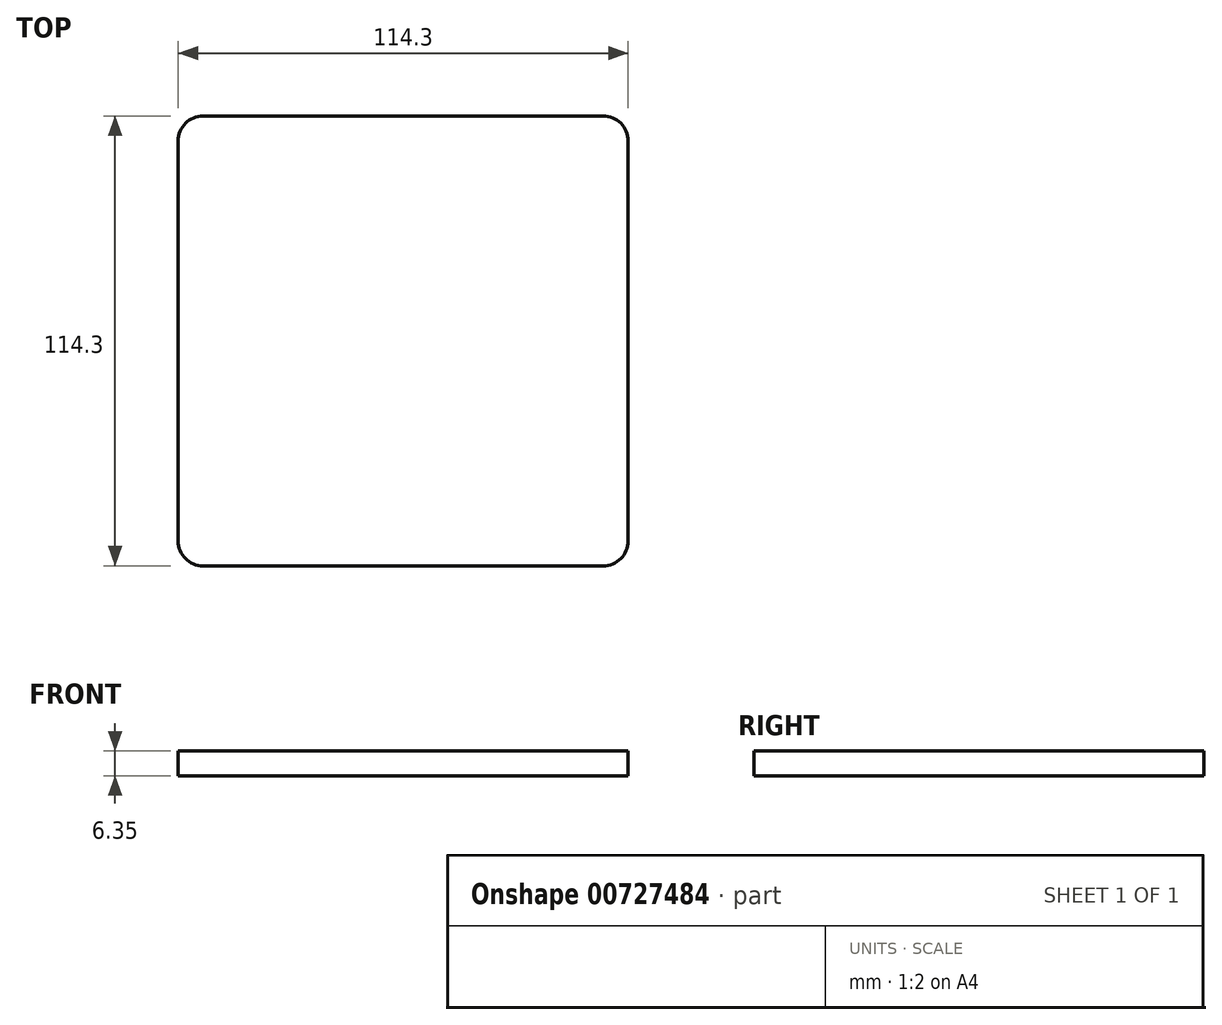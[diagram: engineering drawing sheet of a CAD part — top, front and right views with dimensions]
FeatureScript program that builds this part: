
annotation { "Feature Type Name" : "Feature", "Feature Type Description" : "" }
export const myFeature = defineFeature(function(context is Context, id is Id, definition is map)
    precondition{}
    {
        {
            var Q0;
            Q0=qCreatedBy(makeId("Top.planeOp"),FACE);
            var sketch = newSketch(context, id + "F0", { "sketchPlane" : qUnion([Q0])});
            skLineSegment(sketch, "E0.bottom", {"start": v(50.8, -57.15) * mm, "end": v(-50.8, -57.15) * mm});
            skLineSegment(sketch, "E0.top", {"start": v(50.8, 57.15) * mm, "end": v(-50.8, 57.15) * mm});
            skLineSegment(sketch, "E0.left", {"start": v(57.15, -50.8) * mm, "end": v(57.15, 50.8) * mm});
            skLineSegment(sketch, "E0.right", {"start": v(-57.15, -50.8) * mm, "end": v(-57.15, 50.8) * mm});
            skPoint(sketch, "E0.middle", {"position": v(0, 0) * mm});
            skPoint(sketch, "E1.visualSharp", {"position": v(-57.15, 57.15) * mm});
            skArc(sketch, "E1.filletArc", {"start": v(-50.8, 57.15) * mm, "mid": v(-55.3, 55.3) * mm, "end": v(-57.15, 50.8) * mm});
            skPoint(sketch, "E2.visualSharp", {"position": v(57.15, 57.15) * mm});
            skArc(sketch, "E2.filletArc", {"start": v(57.15, 50.8) * mm, "mid": v(55.3, 55.3) * mm, "end": v(50.8, 57.15) * mm});
            skPoint(sketch, "E3.visualSharp", {"position": v(57.15, -57.15) * mm});
            skArc(sketch, "E3.filletArc", {"start": v(50.8, -57.15) * mm, "mid": v(55.3, -55.3) * mm, "end": v(57.15, -50.8) * mm});
            skPoint(sketch, "E4.visualSharp", {"position": v(-57.15, -57.15) * mm});
            skArc(sketch, "E4.filletArc", {"start": v(-57.15, -50.8) * mm, "mid": v(-55.3, -55.3) * mm, "end": v(-50.8, -57.15) * mm});
            skSolve(sketch);
        }
        {
            var Q0;
            Q0=makeQuery(id+"F0.imprint","IMPRINT",FACE,{"disambiguationData":[TD([[makeQuery(id+"F0.imprint","IMPRINT",EDGE,{"derivedFrom":sQuery(id+"F0.wireOp",EDGE,"E0.bottom")}),-1.0]])]});
            extrude(context, id + "F1", {"entities" : qUnion([Q0]), "depth" : 6.35 * mm, "offsetDistance" : 25.4 * mm});
        }
    });
